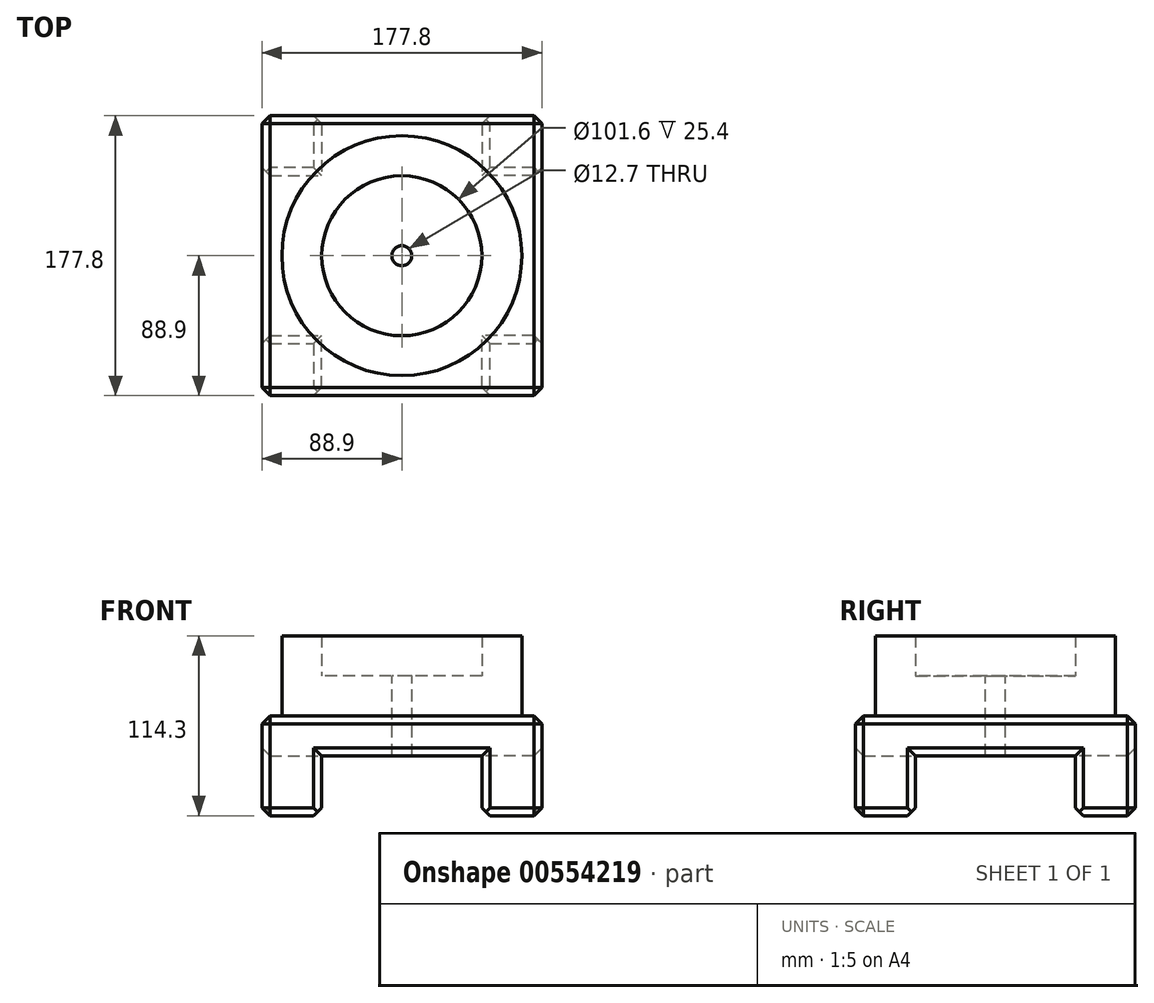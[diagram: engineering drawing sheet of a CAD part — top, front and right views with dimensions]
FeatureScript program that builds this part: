
annotation { "Feature Type Name" : "Feature", "Feature Type Description" : "" }
export const myFeature = defineFeature(function(context is Context, id is Id, definition is map)
    precondition{}
    {
        {
            var Q0;
            Q0=qCreatedBy(makeId("Top.planeOp"),FACE);
            var sketch = newSketch(context, id + "F0", { "sketchPlane" : qUnion([Q0])});
            skCircle(sketch, "E0", {"center": v(0, 0) * mm, "radius": 76.2 * mm});
            skSolve(sketch);
        }
        {
            var Q0;
            Q0 = qSketchRegion(id + "F0", true);
            extrude(context, id + "F1", {"entities" : qUnion([Q0]), "depth" : 25.4 * mm, "offsetDistance" : 25.4 * mm});
        }
        {
            var Q0;
            Q0=makeQuery(id+"F1.opExtrude","CAP_FACE",FACE,{"disambiguationData":[OSD([sQuery(id+"F0.wireOp",EDGE,"E0")])],"isStart":false});
            var sketch = newSketch(context, id + "F2", { "sketchPlane" : qUnion([Q0])});
            skCircle(sketch, "E1", {"center": v(0, 0) * mm, "radius": 50.8 * mm});
            skSolve(sketch);
        }
        {
            var Q0;
            Q0=makeQuery(id+"F2.imprint","IMPRINT",FACE,{"disambiguationData":[TD([[makeQuery(id+"F2.imprint","IMPRINT",EDGE,{"derivedFrom":sQuery(id+"F2.wireOp",EDGE,"E1")}),-1.0]])]});
            extrude(context, id + "F3", {"entities" : qUnion([Q0]), "operationType" : NewBodyOperationType.ADD, "depth" : 25.4 * mm, "offsetDistance" : 25.4 * mm});
        }
        {
            var Q0;
            Q0=makeQuery(id+"F1.opExtrude","CAP_FACE",FACE,{"disambiguationData":[OSD([sQuery(id+"F0.wireOp",EDGE,"E0")])],"isStart":false});
            var sketch = newSketch(context, id + "F4", { "sketchPlane" : qUnion([Q0])});
            skCircle(sketch, "E2", {"center": v(0, 0) * mm, "radius": 6.35 * mm});
            skSolve(sketch);
        }
        {
            var Q0;
            Q0 = qSketchRegion(id + "F4", true);
            extrude(context, id + "F5", {"entities" : qUnion([Q0]), "operationType" : NewBodyOperationType.REMOVE, "oppositeDirection" : true, "depth" : 162.8 * mm, "offsetDistance" : 25.4 * mm});
        }
        {
            var Q0;
            Q0=makeQuery(id+"F1.opExtrude","CAP_FACE",FACE,{"disambiguationData":[OSD([sQuery(id+"F0.wireOp",EDGE,"E0")])],"isStart":true});
            var sketch = newSketch(context, id + "F6", { "sketchPlane" : qUnion([Q0])});
            skLineSegment(sketch, "E3.bottom", {"start": v(-88.9, 88.9) * mm, "end": v(88.9, 88.9) * mm});
            skLineSegment(sketch, "E3.top", {"start": v(-88.9, -88.9) * mm, "end": v(88.9, -88.9) * mm});
            skLineSegment(sketch, "E3.left", {"start": v(-88.9, 88.9) * mm, "end": v(-88.9, -88.9) * mm});
            skLineSegment(sketch, "E3.right", {"start": v(88.9, 88.9) * mm, "end": v(88.9, -88.9) * mm});
            skPoint(sketch, "E3.middle", {"position": v(0, 0) * mm});
            skSolve(sketch);
        }
        {
            var Q0;
            Q0 = qSketchRegion(id + "F6", true);
            extrude(context, id + "F7", {"entities" : qUnion([Q0]), "operationType" : NewBodyOperationType.ADD, "depth" : 25.4 * mm, "offsetDistance" : 25.4 * mm});
        }
        {
            var Q0;
            Q0=makeQuery(id+"F7.opExtrude","CAP_FACE",FACE,{"disambiguationData":[OSD([sQuery(id+"F6.wireOp",EDGE,"E3.bottom"),sQuery(id+"F6.wireOp",EDGE,"E3.top"),sQuery(id+"F6.wireOp",EDGE,"E3.left"),sQuery(id+"F6.wireOp",EDGE,"E3.right")])],"isStart":false});
            var sketch = newSketch(context, id + "F8", { "sketchPlane" : qUnion([Q0])});
            skCircle(sketch, "E4", {"center": v(0, 0) * mm, "radius": 6.35 * mm});
            skSolve(sketch);
        }
        {
            var Q0;
            Q0=makeQuery(id+"F8.imprint","IMPRINT",FACE,{"disambiguationData":[TD([[makeQuery(id+"F8.imprint","IMPRINT",EDGE,{"derivedFrom":sQuery(id+"F8.wireOp",EDGE,"E4")}),1.0]])]});
            extrude(context, id + "F9", {"entities" : qUnion([Q0]), "operationType" : NewBodyOperationType.REMOVE, "oppositeDirection" : true, "depth" : 67.82 * mm, "offsetDistance" : 25.4 * mm});
        }
        {
            var Q0;
            Q0=makeQuery(id+"F7.opExtrude","CAP_FACE",FACE,{"disambiguationData":[OSD([sQuery(id+"F6.wireOp",EDGE,"E3.bottom"),sQuery(id+"F6.wireOp",EDGE,"E3.top"),sQuery(id+"F6.wireOp",EDGE,"E3.left"),sQuery(id+"F6.wireOp",EDGE,"E3.right")])],"isStart":false});
            var sketch = newSketch(context, id + "F10", { "sketchPlane" : qUnion([Q0])});
            skLineSegment(sketch, "E5.bottom", {"start": v(-88.9, 88.9) * mm, "end": v(-50.8, 88.9) * mm});
            skLineSegment(sketch, "E5.top", {"start": v(-88.9, 50.8) * mm, "end": v(-50.8, 50.8) * mm});
            skLineSegment(sketch, "E5.left", {"start": v(-88.9, 88.9) * mm, "end": v(-88.9, 50.8) * mm});
            skLineSegment(sketch, "E5.right", {"start": v(-50.8, 88.9) * mm, "end": v(-50.8, 50.8) * mm});
            skLineSegment(sketch, "E6.bottom", {"start": v(-88.9, -88.9) * mm, "end": v(-50.8, -88.9) * mm});
            skLineSegment(sketch, "E6.top", {"start": v(-88.9, -50.8) * mm, "end": v(-50.8, -50.8) * mm});
            skLineSegment(sketch, "E6.left", {"start": v(-88.9, -88.9) * mm, "end": v(-88.9, -50.8) * mm});
            skLineSegment(sketch, "E6.right", {"start": v(-50.8, -88.9) * mm, "end": v(-50.8, -50.8) * mm});
            skLineSegment(sketch, "E7.bottom", {"start": v(88.9, 88.9) * mm, "end": v(50.8, 88.9) * mm});
            skLineSegment(sketch, "E7.top", {"start": v(88.9, 50.8) * mm, "end": v(50.8, 50.8) * mm});
            skLineSegment(sketch, "E7.left", {"start": v(88.9, 88.9) * mm, "end": v(88.9, 50.8) * mm});
            skLineSegment(sketch, "E7.right", {"start": v(50.8, 88.9) * mm, "end": v(50.8, 50.8) * mm});
            skLineSegment(sketch, "E8.bottom", {"start": v(88.9, -88.9) * mm, "end": v(50.8, -88.9) * mm});
            skLineSegment(sketch, "E8.top", {"start": v(88.9, -50.8) * mm, "end": v(50.8, -50.8) * mm});
            skLineSegment(sketch, "E8.left", {"start": v(88.9, -88.9) * mm, "end": v(88.9, -50.8) * mm});
            skLineSegment(sketch, "E8.right", {"start": v(50.8, -88.9) * mm, "end": v(50.8, -50.8) * mm});
            skSolve(sketch);
        }
        {
            var Q0;
            Q0 = qSketchRegion(id + "F10", true);
            extrude(context, id + "F11", {"entities" : qUnion([Q0]), "operationType" : NewBodyOperationType.ADD, "depth" : 38.1 * mm, "offsetDistance" : 25.4 * mm});
        }
        {
            var Q0;
            Q0=makeQuery(id+"F7.opExtrude","CAP_EDGE",EDGE,{"disambiguationData":[OSD([sQuery(id+"F6.wireOp",EDGE,"E3.bottom")])],"isStart":true});
            var Q1;
            Q1=makeQuery(id+"F7.opExtrude","CAP_EDGE",EDGE,{"disambiguationData":[OSD([sQuery(id+"F6.wireOp",EDGE,"E3.left")])],"isStart":true});
            var Q2;
            Q2=makeQuery(id+"F7.opExtrude","CAP_EDGE",EDGE,{"disambiguationData":[OSD([sQuery(id+"F6.wireOp",EDGE,"E3.right")])],"isStart":true});
            var Q3;
            Q3=makeQuery(id+"F7.opExtrude","CAP_EDGE",EDGE,{"disambiguationData":[OSD([sQuery(id+"F6.wireOp",EDGE,"E3.top")])],"isStart":true});
            var Q4;
            Q4=makeQuery(id+"F11.boolean.opBoolean","MERGE",FACE,{"derivedFrom":[makeQuery(id+"F7.opExtrude","SWEPT_FACE",FACE,{"disambiguationData":[OSD([sQuery(id+"F6.wireOp",EDGE,"E3.bottom")])]}),makeQuery(id+"F11.opExtrude","SWEPT_FACE",FACE,{"disambiguationData":[OSD([sQuery(id+"F10.wireOp",EDGE,"E5.bottom")])]}),makeQuery(id+"F11.opExtrude","SWEPT_FACE",FACE,{"disambiguationData":[OSD([sQuery(id+"F10.wireOp",EDGE,"E7.bottom")])]})]});
            var Q5;
            Q5=makeQuery(id+"F11.boolean.opBoolean","MERGE",FACE,{"derivedFrom":[makeQuery(id+"F7.opExtrude","SWEPT_FACE",FACE,{"disambiguationData":[OSD([sQuery(id+"F6.wireOp",EDGE,"E3.left")])]}),makeQuery(id+"F11.opExtrude","SWEPT_FACE",FACE,{"disambiguationData":[OSD([sQuery(id+"F10.wireOp",EDGE,"E5.left")])]}),makeQuery(id+"F11.opExtrude","SWEPT_FACE",FACE,{"disambiguationData":[OSD([sQuery(id+"F10.wireOp",EDGE,"E6.left")])]})]});
            var Q6;
            Q6=makeQuery(id+"F11.boolean.opBoolean","MERGE",FACE,{"derivedFrom":[makeQuery(id+"F7.opExtrude","SWEPT_FACE",FACE,{"disambiguationData":[OSD([sQuery(id+"F6.wireOp",EDGE,"E3.top")])]}),makeQuery(id+"F11.opExtrude","SWEPT_FACE",FACE,{"disambiguationData":[OSD([sQuery(id+"F10.wireOp",EDGE,"E6.bottom")])]}),makeQuery(id+"F11.opExtrude","SWEPT_FACE",FACE,{"disambiguationData":[OSD([sQuery(id+"F10.wireOp",EDGE,"E8.bottom")])]})]});
            var Q7;
            Q7=makeQuery(id+"F11.boolean.opBoolean","MERGE",FACE,{"derivedFrom":[makeQuery(id+"F7.opExtrude","SWEPT_FACE",FACE,{"disambiguationData":[OSD([sQuery(id+"F6.wireOp",EDGE,"E3.right")])]}),makeQuery(id+"F11.opExtrude","SWEPT_FACE",FACE,{"disambiguationData":[OSD([sQuery(id+"F10.wireOp",EDGE,"E7.left")])]}),makeQuery(id+"F11.opExtrude","SWEPT_FACE",FACE,{"disambiguationData":[OSD([sQuery(id+"F10.wireOp",EDGE,"E8.left")])]})]});
            chamfer(context, id + "F12", {"entities" : qUnion([Q0, Q1, Q2, Q3, Q4, Q5, Q6, Q7]), "width" : 5.08 * mm, "tangentPropagation" : true});
        }
        {
            var Q0;
            Q0=makeQuery(id+"F11.opExtrude","CAP_EDGE",EDGE,{"disambiguationData":[OSD([sQuery(id+"F10.wireOp",EDGE,"E5.right")])],"isStart":false});
            var Q1;
            Q1=makeQuery(id+"F11.opExtrude","CAP_EDGE",EDGE,{"disambiguationData":[OSD([sQuery(id+"F10.wireOp",EDGE,"E5.top")])],"isStart":false});
            var Q2;
            Q2=makeQuery(id+"F11.opExtrude","CAP_EDGE",EDGE,{"disambiguationData":[OSD([sQuery(id+"F10.wireOp",EDGE,"E7.right")])],"isStart":false});
            var Q3;
            Q3=makeQuery(id+"F11.opExtrude","CAP_EDGE",EDGE,{"disambiguationData":[OSD([sQuery(id+"F10.wireOp",EDGE,"E7.top")])],"isStart":false});
            var Q4;
            Q4=makeQuery(id+"F11.opExtrude","CAP_EDGE",EDGE,{"disambiguationData":[OSD([sQuery(id+"F10.wireOp",EDGE,"E6.top")])],"isStart":false});
            var Q5;
            Q5=makeQuery(id+"F11.opExtrude","CAP_EDGE",EDGE,{"disambiguationData":[OSD([sQuery(id+"F10.wireOp",EDGE,"E6.right")])],"isStart":false});
            var Q6;
            Q6=makeQuery(id+"F11.opExtrude","CAP_EDGE",EDGE,{"disambiguationData":[OSD([sQuery(id+"F10.wireOp",EDGE,"E8.top")])],"isStart":false});
            var Q7;
            Q7=makeQuery(id+"F11.opExtrude","CAP_EDGE",EDGE,{"disambiguationData":[OSD([sQuery(id+"F10.wireOp",EDGE,"E8.right")])],"isStart":false});
            chamfer(context, id + "F13", {"entities" : qUnion([Q0, Q1, Q2, Q3, Q4, Q5, Q6, Q7]), "width" : 5.08 * mm, "tangentPropagation" : true});
        }
    });
